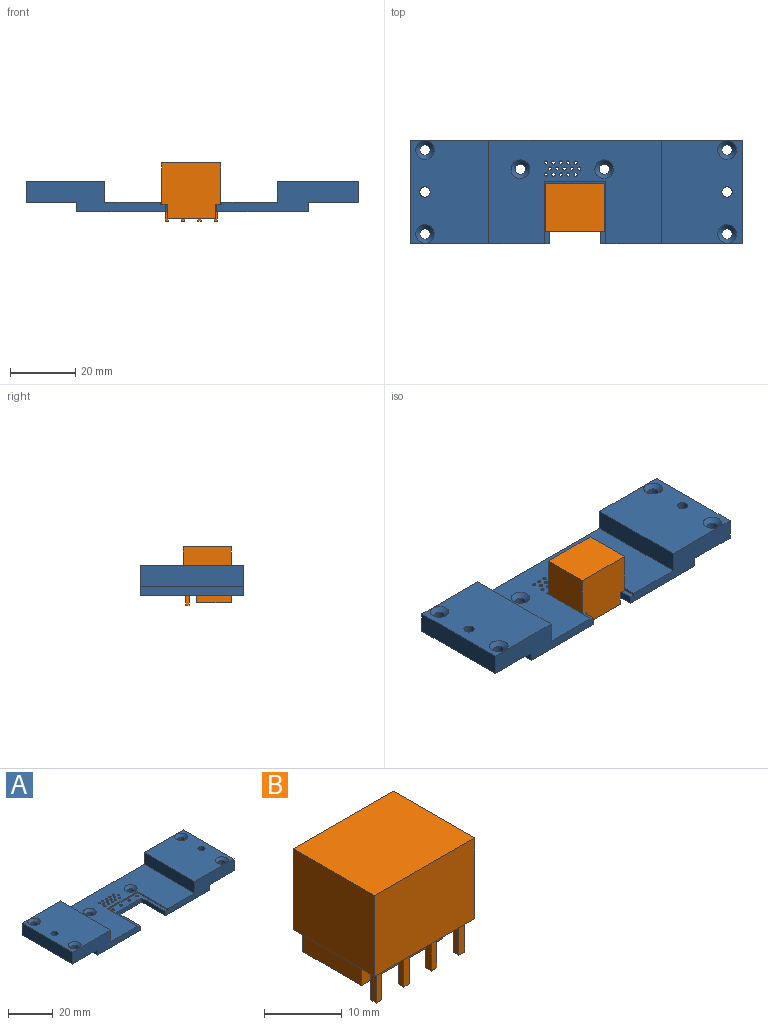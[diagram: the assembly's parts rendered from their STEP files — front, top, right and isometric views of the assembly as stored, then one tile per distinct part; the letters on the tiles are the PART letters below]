
ASSEMBLY  parts=2 mates=1
PART A: 55 faces, bbox 101.6x31.8x9.3 mm
  f0: plane 43.18x9.32mm, normal (0,-1,0), area 239.5mm2, adj f1,f2,f3,f9,f12,f14,f18,f19
  f1: plane 70.84x31.75mm, normal (0,0,-1), area 1983.7mm2, adj f0,f4,f5,f6,f7,f8,f11,f16
  f2: plane 19.05x18.8mm, normal (0,0,1), area 120.6mm2, adj f0,f4,f5,f6,f7,f11,f43,f44
  f3: plane 52.83x31.75mm, normal (0,0,1), area 1255.9mm2, adj f0,f8,f11,f14,f15,f26,f27,f28
  f4: cylinder r=0.66mm len=2.29mm, axis (0,0,1), area 9.5mm2, adj f1,f2
  f5: cylinder r=0.66mm len=2.29mm, axis (0,0,1), area 9.5mm2, adj f1,f2
  f6: cylinder r=0.66mm len=2.29mm, axis (0,0,1), area 9.5mm2, adj f1,f2
  f7: cylinder r=0.66mm len=2.29mm, axis (0,0,1), area 9.5mm2, adj f1,f2
  f8: plane 101.6x9.32mm, normal (0,1,0), area 521.4mm2, adj f1,f3,f9,f10,f12,f13,f14,f15
  f9: plane 31.75x24.64mm, normal (0,0,1), area 723mm2, adj f0,f8,f12,f14,f20,f49,f50
  f10: plane 31.75x6.48mm, normal (-1,0,0), area 205.6mm2, adj f8,f11,f13,f17
  f11: plane 42.67x9.32mm, normal (0,-1,0), area 234mm2, adj f1,f2,f3,f10,f13,f15,f16,f17
  f12: plane 31.75x6.48mm, normal (1,0,0), area 205.6mm2, adj f0,f8,f9,f19
  f13: plane 31.75x24.13mm, normal (0,0,1), area 706.9mm2, adj f8,f10,f11,f15,f24,f53,f54
  f14: plane 31.75x6.4mm, normal (-1,0,0), area 203.2mm2, adj f0,f3,f8,f9
  f15: plane 31.75x6.4mm, normal (1,0,0), area 203.2mm2, adj f3,f8,f11,f13
  f16: plane 31.75x2.84mm, normal (-1,0,0), area 90.3mm2, adj f1,f8,f11,f17
  f17: plane 31.75x15.52mm, normal (0,0,-1), area 469mm2, adj f8,f10,f11,f16,f23,f24,f25
  f18: plane 31.75x2.84mm, normal (1,0,0), area 90.3mm2, adj f0,f1,f8,f19
  f19: plane 31.75x15.24mm, normal (0,0,-1), area 460.1mm2, adj f0,f8,f12,f18,f20,f21,f22
  f20: cylinder r=1.59mm len=6.48mm, axis (0,0,1), area 64.6mm2, adj f9,f19
  f21: cylinder r=1.59mm len=5.21mm, axis (0,0,1), area 51.9mm2, adj f19,f49
  f22: cylinder r=1.59mm len=5.21mm, axis (0,0,1), area 51.9mm2, adj f19,f50
  f23: cylinder r=1.59mm len=5.21mm, axis (0,0,1), area 51.9mm2, adj f17,f53
  f24: cylinder r=1.59mm len=6.48mm, axis (0,0,1), area 64.6mm2, adj f13,f17
  f25: cylinder r=1.59mm len=5.21mm, axis (0,0,1), area 51.9mm2, adj f17,f54
  f26: cylinder r=0.51mm len=2.92mm, axis (0,0,1), area 9.3mm2, adj f1,f3
  f27: cylinder r=0.51mm len=2.92mm, axis (0,0,1), area 9.3mm2, adj f1,f3
  f28: cylinder r=0.51mm len=2.92mm, axis (0,0,1), area 9.3mm2, adj f1,f3
  f29: cylinder r=0.51mm len=2.92mm, axis (0,0,1), area 9.3mm2, adj f1,f3
  f30: cylinder r=1.59mm len=3.18mm, axis (0,0,1), area 16.5mm2, adj f1,f52
  f31: cylinder r=0.51mm len=2.92mm, axis (0,0,1), area 9.3mm2, adj f1,f3
  f32: cylinder r=0.51mm len=2.92mm, axis (0,0,1), area 9.3mm2, adj f1,f3
  f33: cylinder r=0.51mm len=2.92mm, axis (0,0,1), area 9.3mm2, adj f1,f3
  f34: cylinder r=0.51mm len=2.92mm, axis (0,0,1), area 9.3mm2, adj f1,f3
  f35: cylinder r=0.51mm len=2.92mm, axis (0,0,1), area 9.3mm2, adj f1,f3
  f36: cylinder r=0.51mm len=2.92mm, axis (0,0,1), area 9.3mm2, adj f1,f3
  f37: cylinder r=0.51mm len=2.92mm, axis (0,0,1), area 9.3mm2, adj f1,f3
  f38: cylinder r=0.51mm len=2.92mm, axis (0,0,1), area 9.3mm2, adj f1,f3
  f39: cylinder r=0.51mm len=2.92mm, axis (0,0,1), area 9.3mm2, adj f1,f3
  f40: cylinder r=0.51mm len=2.92mm, axis (0,0,1), area 9.3mm2, adj f1,f3
  f41: cylinder r=0.51mm len=2.92mm, axis (0,0,1), area 9.3mm2, adj f1,f3
  f42: cylinder r=1.59mm len=3.18mm, axis (0,0,1), area 16.5mm2, adj f1,f51
  f43: plane 19.05x0.64mm, normal (-1,0,0), area 12.1mm2, adj f0,f2,f3,f44
  f44: plane 18.8x0.64mm, normal (0,-1,0), area 11.9mm2, adj f2,f3,f43,f45
  f45: plane 19.05x0.64mm, normal (1,0,0), area 12.1mm2, adj f2,f3,f11,f44
  f46: plane 14.73x2.29mm, normal (-1,0,0), area 33.7mm2, adj f0,f1,f2,f48
  f47: plane 14.73x2.29mm, normal (1,0,0), area 33.7mm2, adj f1,f2,f11,f48
  f48: plane 15.75x2.29mm, normal (0,-1,0), area 36mm2, adj f1,f2,f46,f47
  f49: cone r=1.59mm half-angle=45deg, axis (0,0,1), area 25.1mm2, adj f9,f21
  f50: cone r=1.59mm half-angle=45deg, axis (0,0,1), area 25.1mm2, adj f9,f22
  f51: cone r=1.59mm half-angle=45deg, axis (0,0,1), area 25.1mm2, adj f3,f42
  f52: cone r=1.59mm half-angle=45deg, axis (0,0,1), area 25.1mm2, adj f3,f30
  f53: cone r=1.59mm half-angle=45deg, axis (0,0,1), area 25.1mm2, adj f13,f23
  f54: cone r=1.59mm half-angle=45deg, axis (0,0,1), area 25.1mm2, adj f13,f25
PART B: 30 faces, bbox 18.2x14.7x17.8 mm
  f0: plane 18.16x14.73mm, normal (0,0,-1), area 106.3mm2, adj f1,f2,f3,f4,f6,f7,f8,f10
  f1: plane 18.16x17.02mm, normal (0,1,0), area 294.3mm2, adj f0,f2,f4,f5,f6,f8,f9
  f2: plane 14.73x12.7mm, normal (-1,0,0), area 187.1mm2, adj f0,f1,f3,f5
  f3: plane 18.16x12.7mm, normal (0,-1,0), area 230.6mm2, adj f0,f2,f4,f5
  f4: plane 14.73x12.7mm, normal (1,0,0), area 187.1mm2, adj f0,f1,f3,f5
  f5: plane 18.16x14.73mm, normal (0,0,1), area 267.5mm2, adj f1,f2,f3,f4
  f6: plane 10.67x4.32mm, normal (1,0,0), area 46.1mm2, adj f0,f1,f7,f9
  f7: plane 14.73x4.32mm, normal (0,-1,0), area 63.6mm2, adj f0,f6,f8,f9
  f8: plane 10.67x4.32mm, normal (-1,0,0), area 46.1mm2, adj f0,f1,f7,f9
  f9: plane 14.73x10.67mm, normal (0,0,-1), area 157.2mm2, adj f1,f6,f7,f8
  f10: plane 5.08x1.02mm, normal (0,1,0), area 5.2mm2, adj f0,f11,f13,f14
  f11: plane 5.08x1.02mm, normal (1,0,0), area 5.2mm2, adj f0,f10,f12,f14
  f12: plane 5.08x1.02mm, normal (0,-1,0), area 5.2mm2, adj f0,f11,f13,f14
  f13: plane 5.08x1.02mm, normal (-1,0,0), area 5.2mm2, adj f0,f10,f12,f14
  f14: plane 1.02x1.02mm, normal (0,0,-1), area 1mm2, adj f10,f11,f12,f13
  f15: plane 5.08x1.02mm, normal (-1,0,0), area 5.2mm2, adj f0,f16,f18,f19
  f16: plane 5.08x1.02mm, normal (0,1,0), area 5.2mm2, adj f0,f15,f17,f19
  f17: plane 5.08x1.02mm, normal (1,0,0), area 5.2mm2, adj f0,f16,f18,f19
  f18: plane 5.08x1.02mm, normal (0,-1,0), area 5.2mm2, adj f0,f15,f17,f19
  f19: plane 1.02x1.02mm, normal (0,0,-1), area 1mm2, adj f15,f16,f17,f18
  f20: plane 5.08x1.02mm, normal (0,1,0), area 5.2mm2, adj f0,f21,f23,f24
  f21: plane 5.08x1.02mm, normal (1,0,0), area 5.2mm2, adj f0,f20,f22,f24
  f22: plane 5.08x1.02mm, normal (0,-1,0), area 5.2mm2, adj f0,f21,f23,f24
  f23: plane 5.08x1.02mm, normal (-1,0,0), area 5.2mm2, adj f0,f20,f22,f24
  f24: plane 1.02x1.02mm, normal (0,0,-1), area 1mm2, adj f20,f21,f22,f23
  f25: plane 5.08x1.02mm, normal (0,1,0), area 5.2mm2, adj f0,f26,f28,f29
  f26: plane 5.08x1.02mm, normal (1,0,0), area 5.2mm2, adj f0,f25,f27,f29
  f27: plane 5.08x1.02mm, normal (0,-1,0), area 5.2mm2, adj f0,f26,f28,f29
  f28: plane 5.08x1.02mm, normal (-1,0,0), area 5.2mm2, adj f0,f25,f27,f29
  f29: plane 1.02x1.02mm, normal (0,0,-1), area 1mm2, adj f25,f26,f27,f28
PLACE A t=(-12.48,-1.2,-3.89)mm
PLACE B rot(axis=(0,0,1),180deg) t=(-12.69,-5.89,-1.6)mm
MATE planar B.f0 <-> A.f2  axis (0,0,-1) through (-5.33,-7.92,-1.6)mm
